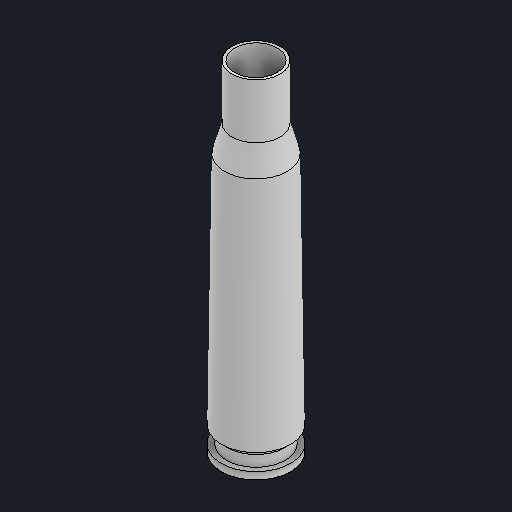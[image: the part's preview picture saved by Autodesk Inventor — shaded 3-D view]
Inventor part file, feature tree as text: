
AUTODESK INVENTOR PART (.ipt)
format: ipt  version: 2025.1 (Build 291241020, 241B)  size: 144,896 bytes
history: native  units: in
note: dims shown in document units (in); Inventor stores cm internally (conversion verified against a paired STEP export)
features: sketch x5, plane x5, extrude x4, draft x1, loft x1, chamfer x1, shell x1, other x1
ambient origin geometry x8: Origin, YZ Plane, XZ Plane, XY Plane, X Axis, Y Axis, Z Axis, Center Point
bodies: Body1 (feature_tree)
feature tree (19):
  sketch  "Sketch5"  dims[d12=0.804in d13=0.083in d14=0.212in d15=3.006in]
  plane  "Work Plane1"
  plane  "Work Plane2"
  plane  "Work Plane3"
  sketch  "Sketch6"  dims[d16=0.68in d17=0.804in]
  sketch  "Sketch7"  dims[d18=3.945in d19=-0.634in d20=0.56in]
  plane  "Work Plane5"
  sketch  "Sketch8"  dims[d21=0.56in d22=0.305in d23=0.0in]
  sketch  "Sketch9"  dims[d24=1.0in d25=0.0in d26=1.0in d27=0.0in d28=0.1061in d29=0.0in d30=90.0deg d31=0.0in d32=90.0deg d33=1.0in d34=0.0in d35=0.062in d36=0.125in d37=45.0deg d38=0.0315in]
  extrude  "Extrusion5"  Depth=0.083in
  extrude  "Extrusion6"  Depth=0.804in
  extrude  "Extrusion7"  Depth=3.945in
  draft  "FaceDraft1"
  loft  "Loft1"
  extrude  "Extrusion8"  Depth=0.0315in TaperAngle=0.0deg
  chamfer  "Chamfer1"  Distance=0.1061in
  shell  "Shell1"  Thickness=0.0in
  plane  "Work Plane4"
  other  "Edges1"
